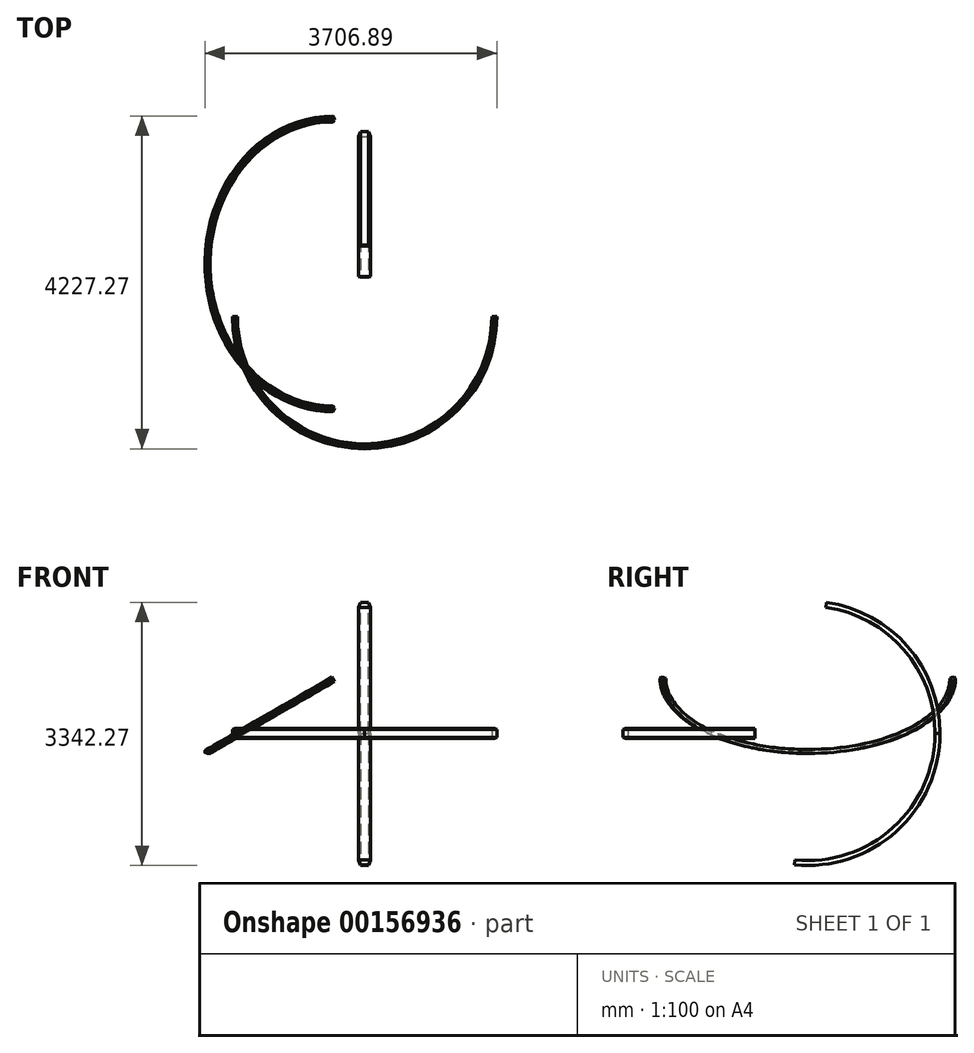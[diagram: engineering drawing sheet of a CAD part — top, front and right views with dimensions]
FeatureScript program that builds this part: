
annotation { "Feature Type Name" : "Feature", "Feature Type Description" : "" }
export const myFeature = defineFeature(function(context is Context, id is Id, definition is map)
    precondition{}
    {
        {
            var Q0;
            Q0=qCreatedBy(makeId("Right.planeOp"),FACE);
            var sketch = newSketch(context, id + "F0", { "sketchPlane" : qUnion([Q0])});
            skLineSegment(sketch, "E0", {"start": v(0, 0) * mm, "end": v(0, -279.4) * mm, "construction": true});
            skLineSegment(sketch, "E1", {"start": v(0, -279.4) * mm, "end": v(457.2, -279.4) * mm, "construction": true});
            skLineSegment(sketch, "E2", {"start": v(457.2, -279.4) * mm, "end": v(457.2, -558.8) * mm, "construction": true});
            skLineSegment(sketch, "E3", {"start": v(0, -279.4) * mm, "end": v(457.2, -558.8) * mm, "construction": true});
            skLineSegment(sketch, "E4", {"start": v(457.2, -558.8) * mm, "end": v(5486.4, -3632.2) * mm, "construction": true});
            skLineSegment(sketch, "E5", {"start": v(4443.01, -3632.2) * mm, "end": v(5486.4, -3632.2) * mm, "construction": true});
            skLineSegment(sketch, "E6", {"start": v(0, -279.4) * mm, "end": v(-283.7, -743.65) * mm, "construction": true});
            skLineSegment(sketch, "E7", {"start": v(-4243.79, 1676.4) * mm, "end": v(0, 1676.4) * mm, "construction": true});
            skLineSegment(sketch, "E8", {"start": v(0, 1676.4) * mm, "end": v(0, 0) * mm, "construction": true});
            skLineSegment(sketch, "E9", {"start": v(4443.01, -3632.2) * mm, "end": v(-3189.74, -3632.2) * mm});
            skPoint(sketch, "E9.endSnap0", {"position": v(4964.7, -3632.2) * mm});
            skLineSegment(sketch, "E10", {"start": v(0, 1676.4) * mm, "end": v(12707.68, 1676.4) * mm, "construction": true});
            skLineSegment(sketch, "E11", {"start": v(-283.7, -743.65) * mm, "end": v(4443.01, -3632.2) * mm, "construction": true});
            skLineSegment(sketch, "E12.MirrorCS", {"start": v(-4243.79, 1676.4) * mm, "end": v(-283.7, -743.65) * mm, "construction": true});
            skPoint(sketch, "E13", {"position": v(-3112.54, 1676.4) * mm});
            skLineSegment(sketch, "E14", {"start": v(-3112.54, 2367.72) * mm, "end": v(-3112.54, 985.08) * mm, "construction": true});
            skLineSegment(sketch, "E15", {"start": v(-4243.79, 1676.4) * mm, "end": v(1635.62, 5269.37) * mm, "construction": true});
            skArc(sketch, "E16", {"start": v(-848.5, -279.4) * mm, "mid": v(-1906.1, 2127.32) * mm, "end": v(0, 3937.72) * mm, "construction": true});
            skLineSegment(sketch, "E17", {"start": v(-1219.2, 0) * mm, "end": v(0, 0) * mm, "construction": true});
            skLineSegment(sketch, "E18.0", {"start": v(-4207.26, 1698.73) * mm, "end": v(5033.26, -3948.26) * mm, "construction": true});
            skArc(sketch, "E19.0", {"start": v(-397.8, -555.9) * mm, "mid": v(-1952.12, 2214.27) * mm, "end": v(673.94, 4001.32) * mm, "construction": true});
            skLineSegment(sketch, "E20", {"start": v(0, -279.4) * mm, "end": v(-457.2, 0) * mm, "construction": true});
            skLineSegment(sketch, "E21", {"start": v(-1434.4, 3123.85) * mm, "end": v(-1434.4, 228.95) * mm, "construction": true});
            skLineSegment(sketch, "E22", {"start": v(334.98, 1676.4) * mm, "end": v(-1434.4, 1676.4) * mm, "construction": true});
            skLineSegment(sketch, "E23", {"start": v(-1434.4, 1676.4) * mm, "end": v(-1951.02, 1676.4) * mm, "construction": true});
            skLineSegment(sketch, "E24", {"start": v(0, 3937.72) * mm, "end": v(0, 1676.4) * mm, "construction": true});
            skArc(sketch, "E25", {"start": v(0, 3937.72) * mm, "mid": v(281.12, 3961.77) * mm, "end": v(563.06, 3951) * mm, "construction": true});
            skLineSegment(sketch, "E26", {"start": v(563.06, 3951) * mm, "end": v(1635.62, 5269.37) * mm, "construction": true});
            skLineSegment(sketch, "E27", {"start": v(-848.5, -279.4) * mm, "end": v(-848.5, 1083.2) * mm});
            skSolve(sketch);
        }
        {
            var Q0;
            Q0=sQuery(id+"F0.wireOp",EDGE,"E16");
            var Q1;
            Q1=sQuery(id+"F0.wireOp",VERTEX,"E23.end");
            cPlane(context, id + "F1", {"entities" : qUnion([Q0, Q1]), "cplaneType" : CPlaneType.CURVE_POINT, "offset" : 25.4 * mm, "width" : 152.4 * mm, "height" : 152.4 * mm});
        }
        {
            var Q0;
            Q0=qCreatedBy(id+"F1.planeOp",FACE);
            var sketch = newSketch(context, id + "F2", { "sketchPlane" : qUnion([Q0])});
            skLineSegment(sketch, "E28", {"start": v(-76.2, -1951.02) * mm, "end": v(76.2, -1951.02) * mm});
            skLineSegment(sketch, "E29", {"start": v(0, -1951.02) * mm, "end": v(0, -2014.52) * mm, "construction": true});
            skPoint(sketch, "E29.endSnap0", {"position": v(0, -1951.02) * mm});
            skLineSegment(sketch, "E30", {"start": v(-76.2, -1951.02) * mm, "end": v(-50.8, -2014.52) * mm});
            skLineSegment(sketch, "E31", {"start": v(-50.8, -2014.52) * mm, "end": v(0, -2014.52) * mm});
            skLineSegment(sketch, "E32.MirrorCS", {"start": v(76.2, -1951.02) * mm, "end": v(50.8, -2014.52) * mm});
            skLineSegment(sketch, "E33.MirrorCS", {"start": v(50.8, -2014.52) * mm, "end": v(0, -2014.52) * mm});
            skSolve(sketch);
        }
        {
            var Q0;
            Q0=qCreatedBy(makeId("Right.planeOp"),FACE);
            var sketch = newSketch(context, id + "F3", { "sketchPlane" : qUnion([Q0])});
            skArc(sketch, "E34", {"start": v(-1951.02, 1676.4) * mm, "mid": v(-1198.7, 3371.57) * mm, "end": v(563.06, 3951) * mm});
            skArc(sketch, "E35", {"start": v(-1951.02, 1676.4) * mm, "mid": v(-1391.74, 178.33) * mm, "end": v(12.42, -586.73) * mm});
            skLineSegment(sketch, "E36", {"start": v(563.06, 3951) * mm, "end": v(334.98, 1676.4) * mm, "construction": true});
            skSolve(sketch);
        }
        {
            var Q0;
            Q0=makeQuery(id+"F2.imprint","IMPRINT",FACE,{"disambiguationData":[TD([[makeQuery(id+"F2.imprint","IMPRINT",EDGE,{"derivedFrom":sQuery(id+"F2.wireOp",EDGE,"E28")}),-1.0]])]});
            var Q1;
            Q1=sQuery(id+"F3.wireOp",EDGE,"E34");
            sweep(context, id + "F4", {"profiles" : qUnion([Q0]), "path" : qUnion([Q1])});
        }
        {
            var Q0;
            Q0=makeQuery(id+"F2.imprint","IMPRINT",FACE,{"disambiguationData":[TD([[makeQuery(id+"F2.imprint","IMPRINT",EDGE,{"derivedFrom":sQuery(id+"F2.wireOp",EDGE,"E28")}),-1.0]])]});
            var Q1;
            Q1=sQuery(id+"F3.wireOp",EDGE,"E35");
            sweep(context, id + "F5", {"profiles" : qUnion([Q0]), "path" : qUnion([Q1])});
        }
        {
            var Q0;
            Q0=qCreatedBy(id+"F1.planeOp",FACE);
            var sketch = newSketch(context, id + "F6", { "sketchPlane" : qUnion([Q0])});
            skArc(sketch, "E37", {"start": v(0, -1951.02) * mm, "mid": v(1616.45, -1281.46) * mm, "end": v(2286, 334.98) * mm});
            skArc(sketch, "E38.MirrorCS", {"start": v(0, -1951.02) * mm, "mid": v(-1616.45, -1281.46) * mm, "end": v(-2286, 334.98) * mm});
            skLineSegment(sketch, "E39", {"start": v(0, 334.98) * mm, "end": v(-2286, 334.98) * mm, "construction": true});
            skSolve(sketch);
        }
        {
            var Q0;
            Q0=sQuery(id+"F6.wireOp",EDGE,"E37");
            var Q1;
            Q1=sQuery(id+"F2.wireOp",VERTEX,"E29.endSnap0");
            cPlane(context, id + "F7", {"entities" : qUnion([Q0, Q1]), "cplaneType" : CPlaneType.CURVE_POINT, "offset" : 25.4 * mm, "width" : 152.4 * mm, "height" : 152.4 * mm});
        }
        {
            var Q0;
            Q0=qCreatedBy(id+"F7.planeOp",FACE);
            var sketch = newSketch(context, id + "F8", { "sketchPlane" : qUnion([Q0])});
            skLineSegment(sketch, "E40", {"start": v(-3457.33, -1513.28) * mm, "end": v(-3304.93, -1513.28) * mm});
            skLineSegment(sketch, "E41", {"start": v(-3381.13, -1513.28) * mm, "end": v(-3381.13, -1576.78) * mm, "construction": true});
            skPoint(sketch, "E41.endSnap0", {"position": v(-3381.13, -1513.28) * mm});
            skLineSegment(sketch, "E42", {"start": v(-3457.33, -1513.28) * mm, "end": v(-3431.83, -1576.78) * mm});
            skLineSegment(sketch, "E43", {"start": v(-3431.83, -1576.78) * mm, "end": v(-3381.13, -1576.78) * mm});
            skLineSegment(sketch, "E44.MirrorCS", {"start": v(-3304.93, -1513.28) * mm, "end": v(-3330.43, -1576.78) * mm});
            skLineSegment(sketch, "E45.MirrorCS", {"start": v(-3330.43, -1576.78) * mm, "end": v(-3381.13, -1576.78) * mm});
            skLineSegment(sketch, "E46", {"start": v(-1951.02, 1739.9) * mm, "end": v(-1951.02, 1612.9) * mm});
            skLineSegment(sketch, "E47", {"start": v(-1982.77, 1739.9) * mm, "end": v(-2014.52, 1727.2) * mm});
            skLineSegment(sketch, "E48", {"start": v(-2014.52, 1727.2) * mm, "end": v(-2014.52, 1625.6) * mm});
            skLineSegment(sketch, "E49", {"start": v(-2014.52, 1625.6) * mm, "end": v(-1982.77, 1612.9) * mm});
            skLineSegment(sketch, "E50", {"start": v(-1951.02, 1676.4) * mm, "end": v(-2014.52, 1676.4) * mm, "construction": true});
            skLineSegment(sketch, "E51", {"start": v(-1951.02, 1739.9) * mm, "end": v(-1982.77, 1739.9) * mm});
            skLineSegment(sketch, "E52.MirrorCS", {"start": v(-1951.02, 1612.9) * mm, "end": v(-1982.77, 1612.9) * mm});
            skPoint(sketch, "E53.orphan", {"position": v(-1951.02, 1752.6) * mm});
            skPoint(sketch, "E54.orphan", {"position": v(-1951.02, 1600.2) * mm});
            skSolve(sketch);
        }
        {
            var Q0;
            Q0=makeQuery(id+"F8.imprint","IMPRINT",FACE,{"disambiguationData":[TD([[makeQuery(id+"F8.imprint","IMPRINT",EDGE,{"derivedFrom":sQuery(id+"F8.wireOp",EDGE,"E46")}),-1.0]])]});
            var Q1;
            Q1=sQuery(id+"F6.wireOp",EDGE,"E37");
            sweep(context, id + "F9", {"profiles" : qUnion([Q0]), "path" : qUnion([Q1])});
        }
        {
            var Q0;
            Q0=makeQuery(id+"F8.imprint","IMPRINT",FACE,{"disambiguationData":[TD([[makeQuery(id+"F8.imprint","IMPRINT",EDGE,{"derivedFrom":sQuery(id+"F8.wireOp",EDGE,"E46")}),-1.0]])]});
            var Q1;
            Q1=sQuery(id+"F6.wireOp",EDGE,"E38.MirrorCS");
            sweep(context, id + "F10", {"profiles" : qUnion([Q0]), "path" : qUnion([Q1])});
        }
        {
            var Q0;
            Q0=sQuery(id+"F0.wireOp",EDGE,"E22");
            cPlane(context, id + "F11", {"entities" : qUnion([Q0]), "cplaneType" : CPlaneType.LINE_ANGLE, "offset" : 25.4 * mm, "angle" : 30 * degree, "width" : 152.4 * mm, "height" : 152.4 * mm});
        }
        {
            var Q0;
            Q0=sQuery(id+"F6.wireOp",VERTEX,"E39.end");
            var Q1;
            Q1=sQuery(id+"F6.wireOp",VERTEX,"E37.end");
            var Q2;
            Q2=sQuery(id+"F0.wireOp",VERTEX,"E25.end");
            cPlane(context, id + "F12", {"entities" : qUnion([Q0, Q1, Q2]), "cplaneType" : CPlaneType.THREE_POINT, "offset" : 25.4 * mm, "width" : 152.4 * mm, "height" : 152.4 * mm});
        }
        {
            var Q0;
            Q0=qCreatedBy(id+"F11.planeOp",FACE);
            var sketch = newSketch(context, id + "F13", { "sketchPlane" : qUnion([Q0])});
            skArc(sketch, "E55", {"start": v(838.2, 1951.02) * mm, "mid": v(2494.62, 1240.48) * mm, "end": v(3121.33, -449.45) * mm});
            skArc(sketch, "E56", {"start": v(838.2, 1951.02) * mm, "mid": v(-737.26, 1321.44) * mm, "end": v(-1444.93, -220.52) * mm});
            skSolve(sketch);
        }
        {
            var Q0;
            Q0=sQuery(id+"F13.wireOp",EDGE,"E55");
            var Q1;
            Q1=sQuery(id+"F13.wireOp",VERTEX,"E55.start");
            cPlane(context, id + "F14", {"entities" : qUnion([Q0, Q1]), "cplaneType" : CPlaneType.CURVE_POINT, "offset" : 25.4 * mm, "width" : 152.4 * mm, "height" : 152.4 * mm});
        }
        {
            var Q0;
            Q0=qCreatedBy(id+"F14.planeOp",FACE);
            var sketch = newSketch(context, id + "F15", { "sketchPlane" : qUnion([Q0])});
            skLineSegment(sketch, "E57", {"start": v(-1951.02, 1477.2) * mm, "end": v(-1951.02, 1426.4) * mm});
            skLineSegment(sketch, "E58", {"start": v(-1982.77, 1426.4) * mm, "end": v(-2014.52, 1439.1) * mm});
            skLineSegment(sketch, "E59", {"start": v(-2014.52, 1439.1) * mm, "end": v(-2014.52, 1464.5) * mm});
            skLineSegment(sketch, "E60", {"start": v(-2014.52, 1464.5) * mm, "end": v(-1982.77, 1477.2) * mm});
            skLineSegment(sketch, "E61", {"start": v(-1951.02, 1451.8) * mm, "end": v(-2014.52, 1451.8) * mm, "construction": true});
            skLineSegment(sketch, "E62", {"start": v(-1951.02, 1477.2) * mm, "end": v(-1982.77, 1477.2) * mm});
            skLineSegment(sketch, "E63.MirrorCS", {"start": v(-1951.02, 1426.4) * mm, "end": v(-1982.77, 1426.4) * mm});
            skSolve(sketch);
        }
        {
            var Q0;
            Q0=makeQuery(id+"F15.imprint","IMPRINT",FACE,{"disambiguationData":[TD([[makeQuery(id+"F15.imprint","IMPRINT",EDGE,{"derivedFrom":sQuery(id+"F15.wireOp",EDGE,"E57")}),-1.0]])]});
            var Q1;
            Q1=sQuery(id+"F13.wireOp",EDGE,"E55");
            sweep(context, id + "F16", {"profiles" : qUnion([Q0]), "path" : qUnion([Q1])});
        }
        {
            var Q0;
            Q0=makeQuery(id+"F15.imprint","IMPRINT",FACE,{"disambiguationData":[TD([[makeQuery(id+"F15.imprint","IMPRINT",EDGE,{"derivedFrom":sQuery(id+"F15.wireOp",EDGE,"E57")}),-1.0]])]});
            var Q1;
            Q1=sQuery(id+"F13.wireOp",EDGE,"E56");
            sweep(context, id + "F17", {"profiles" : qUnion([Q0]), "path" : qUnion([Q1])});
        }
        {
            var Q0;
            Q0=qCreatedBy(id+"F12.planeOp",FACE);
            var sketch = newSketch(context, id + "F18", { "sketchPlane" : qUnion([Q0])});
            skLineSegment(sketch, "E64", {"start": v(-1989.95, 2826.86) * mm, "end": v(-2286, 1764.64) * mm});
            skLineSegment(sketch, "E65", {"start": v(-2315.46, 1772.85) * mm, "end": v(-2019.55, 2835.11) * mm});
            skLineSegment(sketch, "E66", {"start": v(0, 1701.46) * mm, "end": v(683.5, 4153.82) * mm});
            skLineSegment(sketch, "E67", {"start": v(-2286, 1764.64) * mm, "end": v(-2315.46, 1772.85) * mm});
            skLineSegment(sketch, "E68", {"start": v(-1989.95, 2826.86) * mm, "end": v(-2019.55, 2835.11) * mm});
            skLineSegment(sketch, "E69", {"start": v(-2017.41, 2842.8) * mm, "end": v(-2019.55, 2835.11) * mm});
            skLineSegment(sketch, "E70", {"start": v(-2315.46, 1772.85) * mm, "end": v(-2317.75, 1764.64) * mm});
            skPoint(sketch, "E71", {"position": v(-2137.98, 2295.75) * mm});
            skSolve(sketch);
        }
        {
            var Q0;
            Q0=sQuery(id+"F18.wireOp",VERTEX,"E71");
            var Q1;
            Q1=sQuery(id+"F18.wireOp",VERTEX,"E66.start");
            var Q2;
            Q2=sQuery(id+"F6.wireOp",VERTEX,"E38.MirrorCS.start");
            cPlane(context, id + "F19", {"entities" : qUnion([Q0, Q1, Q2]), "cplaneType" : CPlaneType.THREE_POINT, "offset" : 25.4 * mm, "width" : 152.4 * mm, "height" : 152.4 * mm});
        }
        {
            var Q0;
            Q0=sQuery(id+"F0.wireOp",EDGE,"E27");
            cPlane(context, id + "F20", {"entities" : qUnion([Q0]), "cplaneType" : CPlaneType.LINE_ANGLE, "offset" : 25.4 * mm, "angle" : 45 * degree, "width" : 152.4 * mm, "height" : 152.4 * mm});
        }
    });
